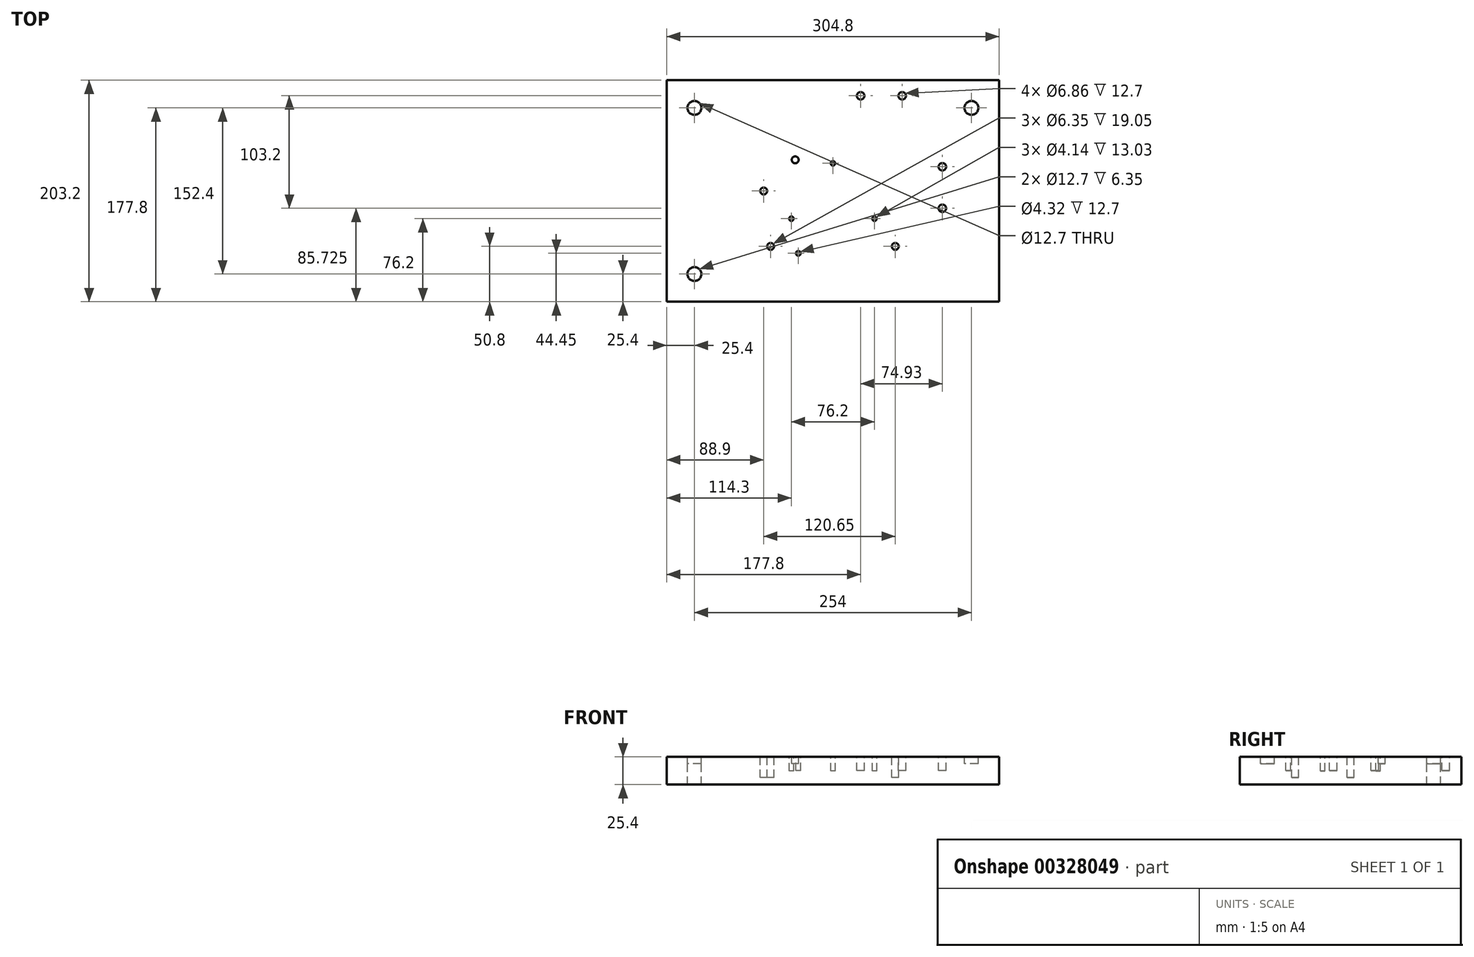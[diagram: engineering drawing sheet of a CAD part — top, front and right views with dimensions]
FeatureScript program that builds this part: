
annotation { "Feature Type Name" : "Feature", "Feature Type Description" : "" }
export const myFeature = defineFeature(function(context is Context, id is Id, definition is map)
    precondition{}
    {
        {
            var Q0;
            Q0=qCreatedBy(makeId("Top.planeOp"),FACE);
            var sketch = newSketch(context, id + "F0", { "sketchPlane" : qUnion([Q0])});
            skLineSegment(sketch, "E0.bottom", {"start": v(-152.4, 101.6) * mm, "end": v(152.4, 101.6) * mm});
            skLineSegment(sketch, "E0.top", {"start": v(-152.4, -101.6) * mm, "end": v(152.4, -101.6) * mm});
            skLineSegment(sketch, "E0.left", {"start": v(-152.4, 101.6) * mm, "end": v(-152.4, -101.6) * mm});
            skLineSegment(sketch, "E0.right", {"start": v(152.4, 101.6) * mm, "end": v(152.4, -101.6) * mm});
            skPoint(sketch, "E0.middle", {"position": v(0, 0) * mm});
            skSolve(sketch);
        }
        {
            var Q0;
            Q0=makeQuery(id+"F0.imprint","IMPRINT",FACE,{"disambiguationData":[TD([[makeQuery(id+"F0.imprint","IMPRINT",EDGE,{"derivedFrom":sQuery(id+"F0.wireOp",EDGE,"E0.bottom")}),-1.0]])]});
            extrude(context, id + "F1", {"entities" : qUnion([Q0]), "depth" : 25.4 * mm});
        }
        {
            var Q0;
            Q0=makeQuery(id+"F1.opExtrude","CAP_FACE",FACE,{"disambiguationData":[OSD([sQuery(id+"F0.wireOp",EDGE,"E0.bottom"),sQuery(id+"F0.wireOp",EDGE,"E0.top"),sQuery(id+"F0.wireOp",EDGE,"E0.left"),sQuery(id+"F0.wireOp",EDGE,"E0.right")])],"isStart":false});
            var sketch = newSketch(context, id + "F2", { "sketchPlane" : qUnion([Q0])});
            skCircle(sketch, "E1", {"center": v(-127, -76.2) * mm, "radius": 6.35 * mm});
            skCircle(sketch, "E2", {"center": v(127, 76.2) * mm, "radius": 6.35 * mm});
            skSolve(sketch);
        }
        {
            var Q0;
            Q0=makeQuery(id+"F2.imprint","IMPRINT",FACE,{"disambiguationData":[TD([[makeQuery(id+"F2.imprint","IMPRINT",EDGE,{"derivedFrom":sQuery(id+"F2.wireOp",EDGE,"E1")}),1.0]])]});
            var Q1;
            Q1=makeQuery(id+"F2.imprint","IMPRINT",FACE,{"disambiguationData":[TD([[makeQuery(id+"F2.imprint","IMPRINT",EDGE,{"derivedFrom":sQuery(id+"F2.wireOp",EDGE,"E2")}),1.0]])]});
            extrude(context, id + "F3", {"entities" : qUnion([Q0, Q1]), "operationType" : NewBodyOperationType.REMOVE, "oppositeDirection" : true, "depth" : 6.35 * mm});
        }
        {
            var Q0;
            Q0=makeQuery(id+"F1.opExtrude","CAP_FACE",FACE,{"disambiguationData":[OSD([sQuery(id+"F0.wireOp",EDGE,"E0.bottom"),sQuery(id+"F0.wireOp",EDGE,"E0.top"),sQuery(id+"F0.wireOp",EDGE,"E0.left"),sQuery(id+"F0.wireOp",EDGE,"E0.right")])],"isStart":false});
            var sketch = newSketch(context, id + "F4", { "sketchPlane" : qUnion([Q0])});
            skCircle(sketch, "E3", {"center": v(-57.15, -50.8) * mm, "radius": 3.17 * mm});
            skCircle(sketch, "E4", {"center": v(57.15, -50.8) * mm, "radius": 3.17 * mm});
            skCircle(sketch, "E5", {"center": v(-63.5, 0) * mm, "radius": 3.17 * mm});
            skSolve(sketch);
        }
        {
            var Q0;
            Q0=makeQuery(id+"F4.imprint","IMPRINT",FACE,{"disambiguationData":[TD([[makeQuery(id+"F4.imprint","IMPRINT",EDGE,{"derivedFrom":sQuery(id+"F4.wireOp",EDGE,"E3")}),1.0]])]});
            var Q1;
            Q1=makeQuery(id+"F4.imprint","IMPRINT",FACE,{"disambiguationData":[TD([[makeQuery(id+"F4.imprint","IMPRINT",EDGE,{"derivedFrom":sQuery(id+"F4.wireOp",EDGE,"E4")}),1.0]])]});
            var Q2;
            Q2=makeQuery(id+"F4.imprint","IMPRINT",FACE,{"disambiguationData":[TD([[makeQuery(id+"F4.imprint","IMPRINT",EDGE,{"derivedFrom":sQuery(id+"F4.wireOp",EDGE,"E5")}),1.0]])]});
            extrude(context, id + "F5", {"entities" : qUnion([Q0, Q1, Q2]), "operationType" : NewBodyOperationType.REMOVE, "oppositeDirection" : true, "depth" : 19.05 * mm});
        }
        {
            var Q0;
            Q0=makeQuery(id+"F1.opExtrude","CAP_FACE",FACE,{"disambiguationData":[OSD([sQuery(id+"F0.wireOp",EDGE,"E0.bottom"),sQuery(id+"F0.wireOp",EDGE,"E0.top"),sQuery(id+"F0.wireOp",EDGE,"E0.left"),sQuery(id+"F0.wireOp",EDGE,"E0.right")])],"isStart":false});
            var sketch = newSketch(context, id + "F6", { "sketchPlane" : qUnion([Q0])});
            skCircle(sketch, "E6", {"center": v(-38.1, -25.4) * mm, "radius": 2.07 * mm});
            skCircle(sketch, "E7", {"center": v(38.1, -25.4) * mm, "radius": 2.07 * mm});
            skCircle(sketch, "E8", {"center": v(0, 25.4) * mm, "radius": 2.07 * mm});
            skSolve(sketch);
        }
        {
            var Q0;
            Q0=makeQuery(id+"F6.imprint","IMPRINT",FACE,{"disambiguationData":[TD([[makeQuery(id+"F6.imprint","IMPRINT",EDGE,{"derivedFrom":sQuery(id+"F6.wireOp",EDGE,"E8")}),1.0]])]});
            var Q1;
            Q1=makeQuery(id+"F6.imprint","IMPRINT",FACE,{"disambiguationData":[TD([[makeQuery(id+"F6.imprint","IMPRINT",EDGE,{"derivedFrom":sQuery(id+"F6.wireOp",EDGE,"E6")}),1.0]])]});
            var Q2;
            Q2=makeQuery(id+"F6.imprint","IMPRINT",FACE,{"disambiguationData":[TD([[makeQuery(id+"F6.imprint","IMPRINT",EDGE,{"derivedFrom":sQuery(id+"F6.wireOp",EDGE,"E7")}),1.0]])]});
            extrude(context, id + "F7", {"entities" : qUnion([Q0, Q1, Q2]), "operationType" : NewBodyOperationType.REMOVE, "oppositeDirection" : true, "depth" : 13.03 * mm});
        }
        {
            var Q0;
            Q0=makeQuery(id+"F1.opExtrude","CAP_FACE",FACE,{"disambiguationData":[OSD([sQuery(id+"F0.wireOp",EDGE,"E0.bottom"),sQuery(id+"F0.wireOp",EDGE,"E0.top"),sQuery(id+"F0.wireOp",EDGE,"E0.left"),sQuery(id+"F0.wireOp",EDGE,"E0.right")])],"isStart":false});
            var sketch = newSketch(context, id + "F8", { "sketchPlane" : qUnion([Q0])});
            skCircle(sketch, "E9", {"center": v(25.4, 87.33) * mm, "radius": 3.43 * mm});
            skCircle(sketch, "E10", {"center": v(63.5, 87.33) * mm, "radius": 3.43 * mm});
            skSolve(sketch);
        }
        {
            var Q0;
            Q0=makeQuery(id+"F8.imprint","IMPRINT",FACE,{"disambiguationData":[TD([[makeQuery(id+"F8.imprint","IMPRINT",EDGE,{"derivedFrom":sQuery(id+"F8.wireOp",EDGE,"E9")}),1.0]])]});
            var Q1;
            Q1=makeQuery(id+"F8.imprint","IMPRINT",FACE,{"disambiguationData":[TD([[makeQuery(id+"F8.imprint","IMPRINT",EDGE,{"derivedFrom":sQuery(id+"F8.wireOp",EDGE,"E10")}),1.0]])]});
            extrude(context, id + "F9", {"entities" : qUnion([Q0, Q1]), "operationType" : NewBodyOperationType.REMOVE, "oppositeDirection" : true, "depth" : 12.7 * mm});
        }
        {
            var Q0;
            Q0=makeQuery(id+"F1.opExtrude","CAP_FACE",FACE,{"disambiguationData":[OSD([sQuery(id+"F0.wireOp",EDGE,"E0.bottom"),sQuery(id+"F0.wireOp",EDGE,"E0.top"),sQuery(id+"F0.wireOp",EDGE,"E0.left"),sQuery(id+"F0.wireOp",EDGE,"E0.right")])],"isStart":false});
            var sketch = newSketch(context, id + "F10", { "sketchPlane" : qUnion([Q0])});
            skCircle(sketch, "E11", {"center": v(-34.62, 28.58) * mm, "radius": 3.18 * mm});
            skSolve(sketch);
        }
        {
            var Q0;
            Q0=makeQuery(id+"F10.imprint","IMPRINT",FACE,{"disambiguationData":[TD([[makeQuery(id+"F10.imprint","IMPRINT",EDGE,{"derivedFrom":sQuery(id+"F10.wireOp",EDGE,"E11")}),1.0]])]});
            extrude(context, id + "F11", {"entities" : qUnion([Q0]), "operationType" : NewBodyOperationType.REMOVE, "oppositeDirection" : true, "depth" : 6.35 * mm});
        }
        {
            var Q0;
            Q0=makeQuery(id+"F1.opExtrude","CAP_FACE",FACE,{"disambiguationData":[OSD([sQuery(id+"F0.wireOp",EDGE,"E0.bottom"),sQuery(id+"F0.wireOp",EDGE,"E0.top"),sQuery(id+"F0.wireOp",EDGE,"E0.left"),sQuery(id+"F0.wireOp",EDGE,"E0.right")])],"isStart":false});
            var sketch = newSketch(context, id + "F12", { "sketchPlane" : qUnion([Q0])});
            skCircle(sketch, "E12", {"center": v(100.33, 22.23) * mm, "radius": 3.43 * mm});
            skCircle(sketch, "E13", {"center": v(100.33, -15.87) * mm, "radius": 3.43 * mm});
            skSolve(sketch);
        }
        {
            var Q0;
            Q0=makeQuery(id+"F12.imprint","IMPRINT",FACE,{"disambiguationData":[TD([[makeQuery(id+"F12.imprint","IMPRINT",EDGE,{"derivedFrom":sQuery(id+"F12.wireOp",EDGE,"E12")}),1.0]])]});
            var Q1;
            Q1=makeQuery(id+"F12.imprint","IMPRINT",FACE,{"disambiguationData":[TD([[makeQuery(id+"F12.imprint","IMPRINT",EDGE,{"derivedFrom":sQuery(id+"F12.wireOp",EDGE,"E13")}),1.0]])]});
            extrude(context, id + "F13", {"entities" : qUnion([Q0, Q1]), "operationType" : NewBodyOperationType.REMOVE, "oppositeDirection" : true, "depth" : 12.7 * mm});
        }
        {
            var Q0;
            Q0=makeQuery(id+"F1.opExtrude","CAP_FACE",FACE,{"disambiguationData":[OSD([sQuery(id+"F0.wireOp",EDGE,"E0.bottom"),sQuery(id+"F0.wireOp",EDGE,"E0.top"),sQuery(id+"F0.wireOp",EDGE,"E0.left"),sQuery(id+"F0.wireOp",EDGE,"E0.right")])],"isStart":false});
            var sketch = newSketch(context, id + "F14", { "sketchPlane" : qUnion([Q0])});
            skCircle(sketch, "E14", {"center": v(-31.75, -57.15) * mm, "radius": 2.16 * mm});
            skSolve(sketch);
        }
        {
            var Q0;
            Q0=makeQuery(id+"F14.imprint","IMPRINT",FACE,{"disambiguationData":[TD([[makeQuery(id+"F14.imprint","IMPRINT",EDGE,{"derivedFrom":sQuery(id+"F14.wireOp",EDGE,"E14")}),1.0]])]});
            extrude(context, id + "F15", {"entities" : qUnion([Q0]), "operationType" : NewBodyOperationType.REMOVE, "oppositeDirection" : true, "depth" : 12.7 * mm});
        }
        {
            var Q0;
            Q0=makeQuery(id+"F1.opExtrude","CAP_FACE",FACE,{"disambiguationData":[OSD([sQuery(id+"F0.wireOp",EDGE,"E0.bottom"),sQuery(id+"F0.wireOp",EDGE,"E0.top"),sQuery(id+"F0.wireOp",EDGE,"E0.left"),sQuery(id+"F0.wireOp",EDGE,"E0.right")])],"isStart":false});
            var sketch = newSketch(context, id + "F16", { "sketchPlane" : qUnion([Q0])});
            skCircle(sketch, "E15", {"center": v(-127, 76.2) * mm, "radius": 6.35 * mm});
            skSolve(sketch);
        }
        {
            var Q0;
            Q0=makeQuery(id+"F16.imprint","IMPRINT",FACE,{"disambiguationData":[TD([[makeQuery(id+"F16.imprint","IMPRINT",EDGE,{"derivedFrom":sQuery(id+"F16.wireOp",EDGE,"E15")}),1.0]])]});
            extrude(context, id + "F17", {"entities" : qUnion([Q0]), "operationType" : NewBodyOperationType.REMOVE, "oppositeDirection" : true, "depth" : 25.4 * mm});
        }
    });
